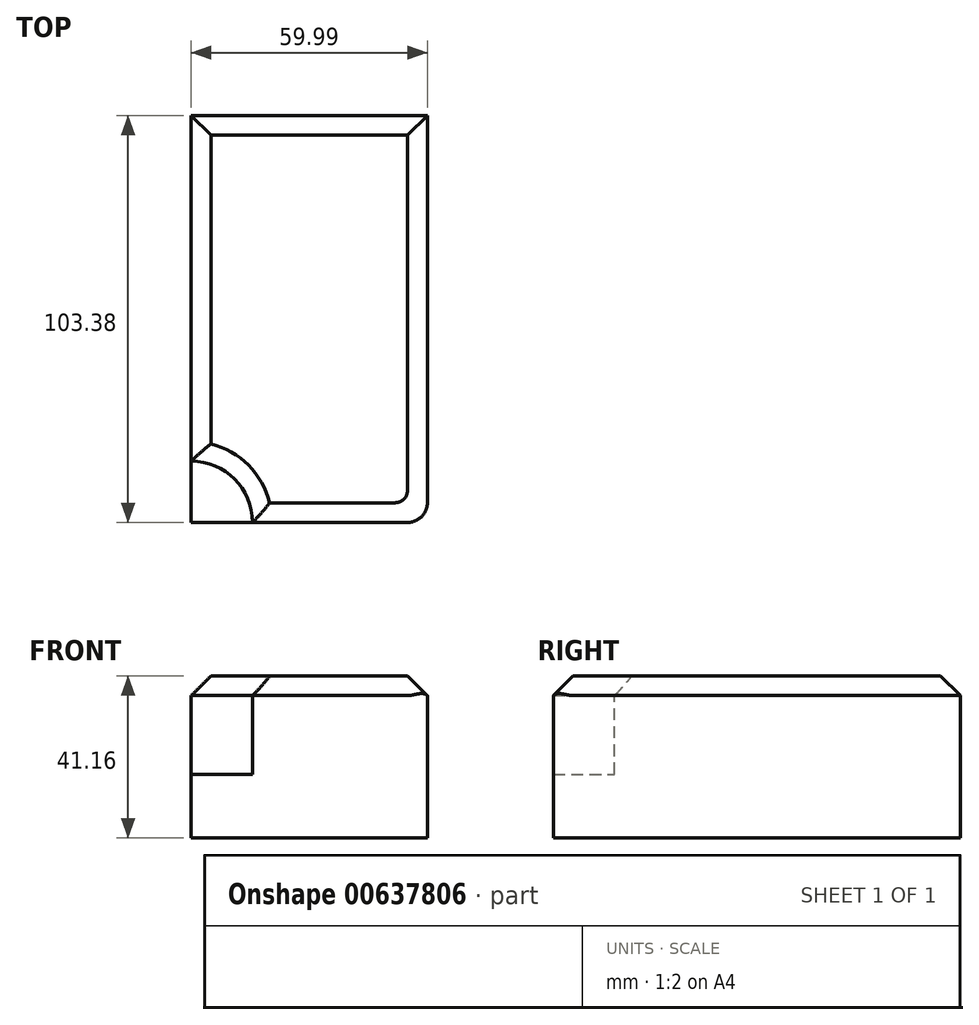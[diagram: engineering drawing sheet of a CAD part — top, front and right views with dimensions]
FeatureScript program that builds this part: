
annotation { "Feature Type Name" : "Feature", "Feature Type Description" : "" }
export const myFeature = defineFeature(function(context is Context, id is Id, definition is map)
    precondition{}
    {
        {
            var Q0;
            Q0=qCreatedBy(makeId("Front.planeOp"),FACE);
            var sketch = newSketch(context, id + "F0", { "sketchPlane" : qUnion([Q0])});
            skLineSegment(sketch, "E0.bottom", {"start": v(0, 0) * mm, "end": v(60, 0) * mm});
            skLineSegment(sketch, "E0.top", {"start": v(0, 41.16) * mm, "end": v(60, 41.16) * mm});
            skLineSegment(sketch, "E0.left", {"start": v(0, 0) * mm, "end": v(0, 41.16) * mm});
            skLineSegment(sketch, "E0.right", {"start": v(60, 0) * mm, "end": v(60, 41.16) * mm});
            skSolve(sketch);
        }
        {
            var Q0;
            Q0 = qSketchRegion(id + "F0", true);
            extrude(context, id + "F1", {"entities" : qUnion([Q0]), "depth" : 103.38 * mm, "offsetDistance" : 25.4 * mm});
        }
        {
            var Q0;
            Q0=makeQuery(id+"F1.opExtrude","SWEPT_FACE",FACE,{"disambiguationData":[OSD([sQuery(id+"F0.wireOp",EDGE,"E0.top")])]});
            var sketch = newSketch(context, id + "F2", { "sketchPlane" : qUnion([Q0])});
            skCircle(sketch, "E1", {"center": v(0, -103.38) * mm, "radius": 15.56 * mm});
            skSolve(sketch);
        }
        {
            var Q0;
            {var subQ0=sQuery(id+"F2.wireOp",EDGE,"E1");var subQ1=sQuery(id+"F0.wireOp",EDGE,"E0.top");var subQ4=makeQuery(id+"F1.opExtrude","CAP_EDGE",EDGE,{"disambiguationData":[OSD([subQ1])],"isStart":false});var subQ5=makeQuery(id+"F2.imprint","INTERSECT",VERTEX,{"derivedFrom":[subQ4,subQ0]});Q0=makeQuery(id+"F2.imprint","IMPRINT",FACE,{"disambiguationData":[TD([[makeQuery(id+"F2.imprint","IMPRINT",EDGE,{"disambiguationData":[TD([[subQ5,1.0]])],"derivedFrom":subQ0}),1.0]])]});}
            var Q1;
            {var subQ0=sQuery(id+"F2.wireOp",EDGE,"E1");var subQ1=sQuery(id+"F0.wireOp",EDGE,"E0.top");var subQ4=makeQuery(id+"F1.opExtrude","CAP_EDGE",EDGE,{"disambiguationData":[OSD([subQ1])],"isStart":false});var subQ5=makeQuery(id+"F2.imprint","INTERSECT",VERTEX,{"derivedFrom":[subQ4,subQ0]});Q1=makeQuery(id+"F2.imprint","IMPRINT",FACE,{"disambiguationData":[TD([[makeQuery(id+"F2.imprint","IMPRINT",EDGE,{"disambiguationData":[TD([[subQ5,-1.0]])],"derivedFrom":subQ0}),1.0]])]});}
            extrude(context, id + "F3", {"entities" : qUnion([Q0, Q1]), "operationType" : NewBodyOperationType.REMOVE, "oppositeDirection" : true, "depth" : 25 * mm, "offsetDistance" : 25 * mm});
        }
        {
            var Q0;
            Q0=makeQuery(id+"F1.opExtrude","SWEPT_FACE",FACE,{"disambiguationData":[OSD([sQuery(id+"F0.wireOp",EDGE,"E0.top")])]});
            chamfer(context, id + "F4", {"entities" : qUnion([Q0]), "width" : 5 * mm, "tangentPropagation" : true});
        }
        {
            var Q0;
            Q0=makeQuery(id+"F1.opExtrude","CAP_EDGE",EDGE,{"disambiguationData":[OSD([sQuery(id+"F0.wireOp",EDGE,"E0.right")])],"isStart":false});
            var Q1;
            {var subQ0=sQuery(id+"F0.wireOp",EDGE,"E0.top");Q1=makeQuery(id+"F4.opChamfer","BLEND_EDGE",EDGE,{"blendedFrom":[makeQuery(id+"F1.opExtrude","SWEPT_EDGE",EDGE,{"disambiguationData":[OSD([subQ0,sQuery(id+"F0.wireOp",EDGE,"E0.right")])]}),makeQuery(id+"F1.opExtrude","CAP_EDGE",EDGE,{"disambiguationData":[OSD([subQ0])],"isStart":false})],"blendedInto":[]});}
            fillet(context, id + "F5", {"entities" : qUnion([Q0, Q1]), "radius" : 5 * mm, "tangentPropagation" : true, "allowEdgeOverflow" : false});
        }
    });
